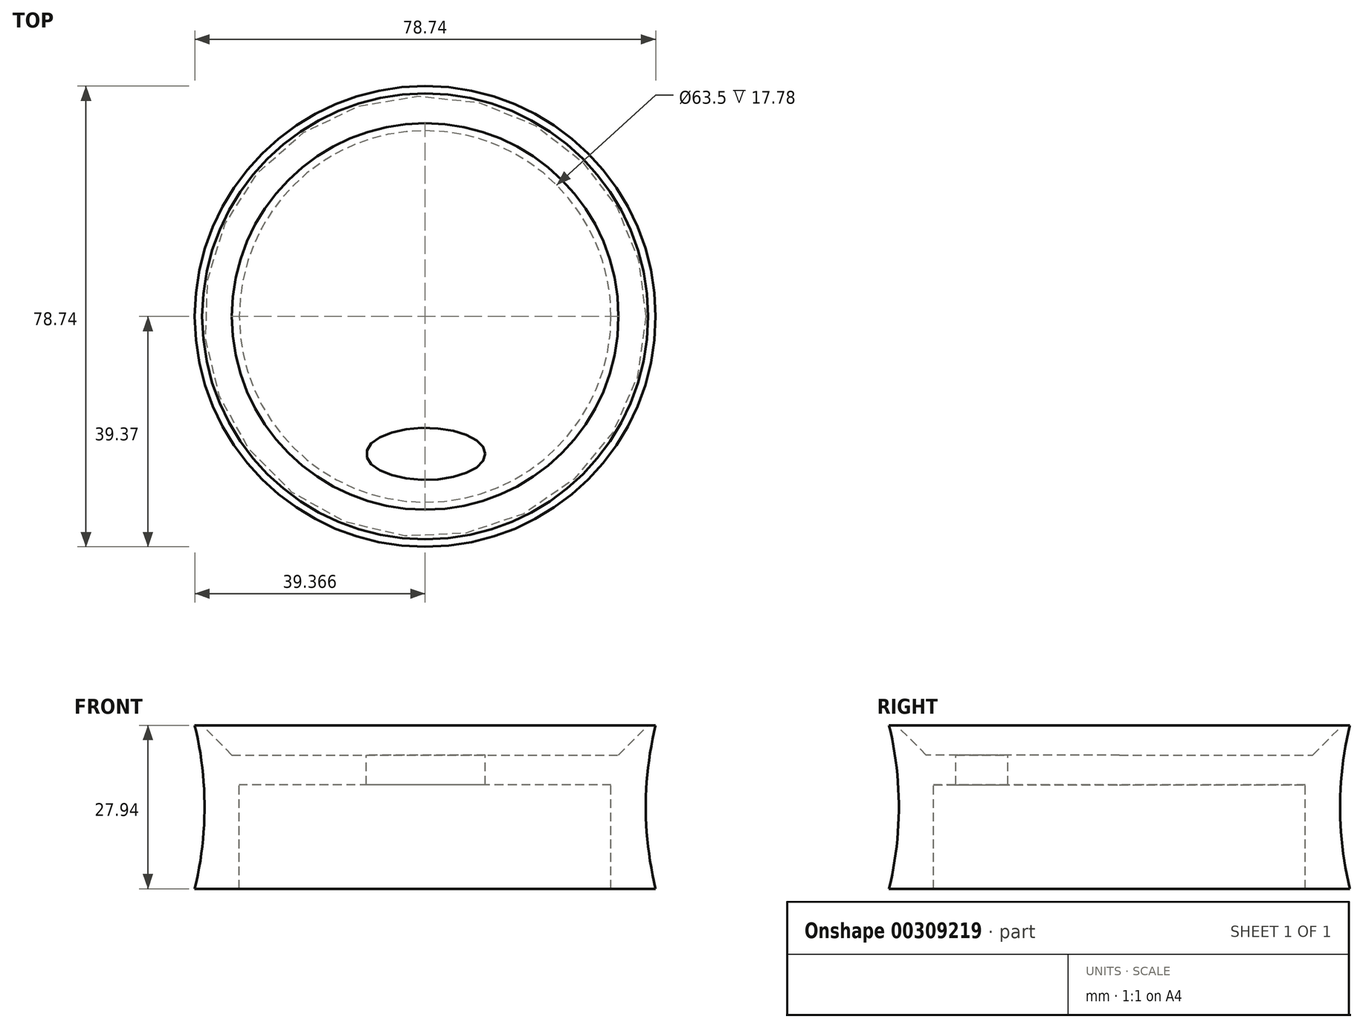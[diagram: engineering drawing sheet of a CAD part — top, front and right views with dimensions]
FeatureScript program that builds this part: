
annotation { "Feature Type Name" : "Feature", "Feature Type Description" : "" }
export const myFeature = defineFeature(function(context is Context, id is Id, definition is map)
    precondition{}
    {
        {
            var Q0;
            Q0=qCreatedBy(makeId("Front.planeOp"),FACE);
            var sketch = newSketch(context, id + "F0", { "sketchPlane" : qUnion([Q0])});
            skLineSegment(sketch, "E0", {"start": v(-31.86, -37.75) * mm, "end": v(-39.48, -37.75) * mm});
            skLineSegment(sketch, "E1", {"start": v(-31.86, -37.75) * mm, "end": v(-31.86, -19.97) * mm});
            skLineSegment(sketch, "E2", {"start": v(-35.67, -14.89) * mm, "end": v(-0.11, -14.89) * mm});
            skLineSegment(sketch, "E3", {"start": v(-35.67, -14.89) * mm, "end": v(-35.67, -9.8) * mm});
            skLineSegment(sketch, "E4", {"start": v(-35.67, -9.8) * mm, "end": v(-39.48, -9.8) * mm});
            skArc(sketch, "E5", {"start": v(-39.48, -37.75) * mm, "mid": v(-37.8, -23.78) * mm, "end": v(-39.48, -9.8) * mm});
            skLineSegment(sketch, "E6", {"start": v(-31.86, -19.97) * mm, "end": v(-0.11, -19.97) * mm});
            skLineSegment(sketch, "E7", {"start": v(-0.11, -14.89) * mm, "end": v(-0.11, -19.97) * mm});
            skSolve(sketch);
        }
        {
            var Q0;
            Q0 = qSketchRegion(id + "F0", true);
            var Q1;
            Q1=sQuery(id+"F0.wireOp",EDGE,"E7");
            revolve(context, id + "F1", {"entities" : qUnion([Q0]), "axis" : qUnion([Q1]), "revolveType" : RevolveType.FULL});
        }
        {
            var Q0;
            Q0=qCreatedBy(makeId("Top.planeOp"),FACE);
            var sketch = newSketch(context, id + "F2", { "sketchPlane" : qUnion([Q0])});
            skEllipse(sketch, "E8", {"center": v(0, -23.5) * mm, "majorRadius": 10.16 * mm, "minorRadius": 4.45 * mm, "majorAxis": v(1, 0)});
            skSolve(sketch);
        }
        {
            var Q0;
            Q0 = qSketchRegion(id + "F2", true);
            extrude(context, id + "F3", {"entities" : qUnion([Q0]), "operationType" : NewBodyOperationType.REMOVE, "oppositeDirection" : true, "depth" : 65.8 * mm});
        }
        {
            var Q0;
            Q0=makeQuery(id+"F1.opRevolve","SWEPT_FACE",FACE,{"disambiguationData":[OSD([sQuery(id+"F0.wireOp",EDGE,"E3")])]});
            chamfer(context, id + "F4", {"entities" : qUnion([Q0]), "width" : 2.54 * mm, "tangentPropagation" : true});
        }
    });
